# Revit family: BIM_KUBAIR F400 CC INTZ Vertical
name_source: partatom
category: Equipement de génie climatique
revit_build: Autodesk Revit 2016 (Build: 20161004_0715(x64)
units: mm (PartAtom-declared; Revit-internal decimal feet)

## family parameters
Basée sur le plan de construction = Non
Cote de connecteur circulaire = Utiliser le diamètre
Couper avec des vides une fois chargée = Non
Numéro OmniClass = 23.75.00.00
Partagée = Non
Point de calcul de pièce = Oui
Titre OmniClass = Climate Control (HVAC)
Toujours verticalement = Oui
Type d'élément = Normal

## types (75) — shared parameters
Classe_de_protection_electrique = F
Consignes – raccordements aérauliques = Raccorder 1, 2 ou 3 ouies  au refoulement et 1, 2 ou 3 ouies à l’aspiration
Fabricant = VIM
G = 31 mm  [stored 0.101706 ft]
Hauteur_equerre = 200 mm  [stored 0.656168 ft]
IfcExportAs = IfcFan
IfcExportType = IfcFlowMovingDevice
Largeur_equerre = 218 mm  [stored 0.715223 ft]
Lien_page_produit = http://www.vim.fr
Materiau_caisson = Acier, galvanisé
Protection_IP = IP 55
Visibilité_marque = Oui

## per-type parameters (varying)
| type | A | BVC | C | Code_article | Courant_nominal | D | Debit_maxi | Debit_mini | GC | H | L | Modèle | Nombre_de_phases | Poids | Position_A_equerre | Prof_INTZ | Puissance_electrique | Tension_nominale |
| KUBAIR F400 CC 355 6PM INTZ 0,18kW | 627 mm  [stored 2.05709 ft] | 645 mm  [stored 2.11614 ft] | 263 mm  [stored 0.862861 ft] | 644537 | 2 A | 559 mm  [stored 1.83399 ft] | 2140 m³/h | 620 m³/h | 50 mm  [stored 0.164042 ft] | 315 mm  [stored 1.03346 ft] | 321 mm  [stored 1.05315 ft] | KUBAIR F400 CC 355 6PM INTZ 0,18kW Caisson | 1 | 59 Kg | 155 mm  [stored 0.50853 ft] | 100 mm  [stored 0.328084 ft] | 180 W | 230 V |
| KUBAIR F400 CC 355 4PM INTZ 0,25kW | 627 mm  [stored 2.05709 ft] | 645 mm  [stored 2.11614 ft] | 263 mm  [stored 0.862861 ft] | 644533 | 3 A | 559 mm  [stored 1.83399 ft] | 3090 m³/h | 900 m³/h | 50 mm  [stored 0.164042 ft] | 315 mm  [stored 1.03346 ft] | 321 mm  [stored 1.05315 ft] | KUBAIR F400 CC 355 4PM INTZ 0,25kW Caisson | 1 | 59 Kg | 155 mm  [stored 0.50853 ft] | 100 mm  [stored 0.328084 ft] | 250 W | 230 V |
| KUBAIR F400 CC 355 4PT IE1 INTZ 0,25kW | 627 mm  [stored 2.05709 ft] | 645 mm  [stored 2.11614 ft] | 263 mm  [stored 0.862861 ft] | 644541 | 1 A | 559 mm  [stored 1.83399 ft] | 3090 m³/h | 900 m³/h | 50 mm  [stored 0.164042 ft] | 315 mm  [stored 1.03346 ft] | 321 mm  [stored 1.05315 ft] | KUBAIR F400 CC 355 4PT IE1 INTZ 0,25kW Caisson | 3 | 59 Kg | 155 mm  [stored 0.50853 ft] | 100 mm  [stored 0.328084 ft] | 250 W | 400 V |
| KUBAIR F400 CC 355 4PT IE2 INTZ 0,25kW | 627 mm  [stored 2.05709 ft] | 645 mm  [stored 2.11614 ft] | 263 mm  [stored 0.862861 ft] | 644545 | 1 A | 559 mm  [stored 1.83399 ft] | 3090 m³/h | 900 m³/h | 50 mm  [stored 0.164042 ft] | 315 mm  [stored 1.03346 ft] | 321 mm  [stored 1.05315 ft] | KUBAIR F400 CC 355 4PT IE2 INTZ 0,25kW Caisson | 3 | 59 Kg | 155 mm  [stored 0.50853 ft] | 100 mm  [stored 0.328084 ft] | 250 W | 400 V |
| KUBAIR F400 CC 355 4PT IE3 INTZ 0,25kW | 627 mm  [stored 2.05709 ft] | 645 mm  [stored 2.11614 ft] | 263 mm  [stored 0.862861 ft] | 644549 | 1 A | 559 mm  [stored 1.83399 ft] | 3090 m³/h | 900 m³/h | 50 mm  [stored 0.164042 ft] | 315 mm  [stored 1.03346 ft] | 321 mm  [stored 1.05315 ft] | KUBAIR F400 CC 355 4PT IE3 INTZ 0,25kW Caisson | 3 | 59 Kg | 155 mm  [stored 0.50853 ft] | 100 mm  [stored 0.328084 ft] | 250 W | 400 V |
| KUBAIR F400 CC 355 6PT IE1 INTZ 0,18kW | 627 mm  [stored 2.05709 ft] | 645 mm  [stored 2.11614 ft] | 263 mm  [stored 0.862861 ft] | 644553 | 1 A | 559 mm  [stored 1.83399 ft] | 2140 m³/h | 620 m³/h | 50 mm  [stored 0.164042 ft] | 315 mm  [stored 1.03346 ft] | 321 mm  [stored 1.05315 ft] | KUBAIR F400 CC 355 6PT IE1 INTZ 0,18kW Caisson | 3 | 59 Kg | 155 mm  [stored 0.50853 ft] | 100 mm  [stored 0.328084 ft] | 180 W | 400 V |
| KUBAIR F400 CC 355 6PT IE2 INTZ 0,18kW | 627 mm  [stored 2.05709 ft] | 645 mm  [stored 2.11614 ft] | 263 mm  [stored 0.862861 ft] | 644557 | 1 A | 559 mm  [stored 1.83399 ft] | 2140 m³/h | 620 m³/h | 50 mm  [stored 0.164042 ft] | 315 mm  [stored 1.03346 ft] | 321 mm  [stored 1.05315 ft] | KUBAIR F400 CC 355 6PT IE2 INTZ 0,18kW Caisson | 3 | 59 Kg | 155 mm  [stored 0.50853 ft] | 100 mm  [stored 0.328084 ft] | 180 W | 400 V |
| KUBAIR F400 CC 355 6PT IE3 INTZ 0,18kW | 627 mm  [stored 2.05709 ft] | 645 mm  [stored 2.11614 ft] | 263 mm  [stored 0.862861 ft] | 644561 | 1 A | 559 mm  [stored 1.83399 ft] | 2140 m³/h | 620 m³/h | 50 mm  [stored 0.164042 ft] | 315 mm  [stored 1.03346 ft] | 321 mm  [stored 1.05315 ft] | KUBAIR F400 CC 355 6PT IE3 INTZ 0,18kW Caisson | 3 | 59 Kg | 155 mm  [stored 0.50853 ft] | 100 mm  [stored 0.328084 ft] | 180 W | 400 V |
| KUBAIR F400 CC 355 4/6PT INTZ 0,30/0,10kW | 627 mm  [stored 2.05709 ft] | 645 mm  [stored 2.11614 ft] | 263 mm  [stored 0.862861 ft] | 644565 | 1 A | 559 mm  [stored 1.83399 ft] | 3090 m³/h | 900 m³/h | 50 mm  [stored 0.164042 ft] | 315 mm  [stored 1.03346 ft] | 321 mm  [stored 1.05315 ft] | KUBAIR F400 CC 355 4/6PT INTZ 0,30/0,10kW Caisson | 3 | 61 Kg | 155 mm  [stored 0.50853 ft] | 100 mm  [stored 0.328084 ft] | 300 W | 400 V |
| KUBAIR F400 CC 355 4/8PT INTZ 0,60/0,15kW | 627 mm  [stored 2.05709 ft] | 645 mm  [stored 2.11614 ft] | 263 mm  [stored 0.862861 ft] | 644569 | 2 A | 559 mm  [stored 1.83399 ft] | 3090 m³/h | 900 m³/h | 50 mm  [stored 0.164042 ft] | 315 mm  [stored 1.03346 ft] | 321 mm  [stored 1.05315 ft] | KUBAIR F400 CC 355 4/8PT INTZ 0,60/0,15kW Caisson | 3 | 61 Kg | 155 mm  [stored 0.50853 ft] | 100 mm  [stored 0.328084 ft] | 600 W | 400 V |
| KUBAIR F400 CC 400 4PM INTZ 0,55kW | 699 mm  [stored 2.29331 ft] | 678 mm  [stored 2.22441 ft] | 297 mm  [stored 0.974409 ft] | 644573 | 4 A | 631 mm  [stored 2.07021 ft] | 5000 m³/h | 1060 m³/h | 50 mm  [stored 0.164042 ft] | 349 mm  [stored 1.14501 ft] | 321 mm  [stored 1.05315 ft] | KUBAIR F400 CC 400 4PM INTZ 0,55kW Caisson | 1 | 72 Kg | 155 mm  [stored 0.50853 ft] | 120 mm  [stored 0.393701 ft] | 550 W | 230 V |
| KUBAIR F400 CC 400 6PM INTZ 0,25kW | 699 mm  [stored 2.29331 ft] | 678 mm  [stored 2.22441 ft] | 297 mm  [stored 0.974409 ft] | 644577 | 2 A | 631 mm  [stored 2.07021 ft] | 3310 m³/h | 520 m³/h | 50 mm  [stored 0.164042 ft] | 349 mm  [stored 1.14501 ft] | 321 mm  [stored 1.05315 ft] | KUBAIR F400 CC 400 6PM INTZ 0,25kW Caisson | 1 | 72 Kg | 155 mm  [stored 0.50853 ft] | 120 mm  [stored 0.393701 ft] | 250 W | 230 V |
| KUBAIR F400 CC 400 4PT IE1 INTZ 0,55kW | 699 mm  [stored 2.29331 ft] | 678 mm  [stored 2.22441 ft] | 297 mm  [stored 0.974409 ft] | 644581 | 1 A | 631 mm  [stored 2.07021 ft] | 5000 m³/h | 1060 m³/h | 50 mm  [stored 0.164042 ft] | 349 mm  [stored 1.14501 ft] | 321 mm  [stored 1.05315 ft] | KUBAIR F400 CC 400 4PT IE1 INTZ 0,55kW Caisson | 3 | 72 Kg | 155 mm  [stored 0.50853 ft] | 120 mm  [stored 0.393701 ft] | 550 W | 400 V |
| KUBAIR F400 CC 400 4PT IE2 INTZ 0,55kW | 699 mm  [stored 2.29331 ft] | 678 mm  [stored 2.22441 ft] | 297 mm  [stored 0.974409 ft] | 644585 | 1 A | 631 mm  [stored 2.07021 ft] | 5000 m³/h | 1060 m³/h | 50 mm  [stored 0.164042 ft] | 349 mm  [stored 1.14501 ft] | 321 mm  [stored 1.05315 ft] | KUBAIR F400 CC 400 4PT IE2 INTZ 0,55kW Caisson | 3 | 72 Kg | 155 mm  [stored 0.50853 ft] | 120 mm  [stored 0.393701 ft] | 550 W | 400 V |
| KUBAIR F400 CC 400 4PT IE3 INTZ 0,55kW | 699 mm  [stored 2.29331 ft] | 678 mm  [stored 2.22441 ft] | 297 mm  [stored 0.974409 ft] | 644589 | 1 A | 631 mm  [stored 2.07021 ft] | 5000 m³/h | 1060 m³/h | 50 mm  [stored 0.164042 ft] | 349 mm  [stored 1.14501 ft] | 321 mm  [stored 1.05315 ft] | KUBAIR F400 CC 400 4PT IE3 INTZ 0,55kW Caisson | 3 | 72 Kg | 155 mm  [stored 0.50853 ft] | 120 mm  [stored 0.393701 ft] | 550 W | 400 V |
| KUBAIR F400 CC 400 6PT IE1 INTZ 0,37kW | 699 mm  [stored 2.29331 ft] | 678 mm  [stored 2.22441 ft] | 297 mm  [stored 0.974409 ft] | 644593 | 1 A | 631 mm  [stored 2.07021 ft] | 3310 m³/h | 520 m³/h | 50 mm  [stored 0.164042 ft] | 349 mm  [stored 1.14501 ft] | 321 mm  [stored 1.05315 ft] | KUBAIR F400 CC 400 6PT IE1 INTZ 0,37kW Caisson | 3 | 72 Kg | 155 mm  [stored 0.50853 ft] | 120 mm  [stored 0.393701 ft] | 370 W | 400 V |
| KUBAIR F400 CC 400 6PT IE2 INTZ 0,37kW | 699 mm  [stored 2.29331 ft] | 678 mm  [stored 2.22441 ft] | 297 mm  [stored 0.974409 ft] | 644597 | 1 A | 631 mm  [stored 2.07021 ft] | 3310 m³/h | 520 m³/h | 50 mm  [stored 0.164042 ft] | 349 mm  [stored 1.14501 ft] | 321 mm  [stored 1.05315 ft] | KUBAIR F400 CC 400 6PT IE2 INTZ 0,37kW Caisson | 3 | 72 Kg | 155 mm  [stored 0.50853 ft] | 120 mm  [stored 0.393701 ft] | 370 W | 400 V |
| KUBAIR F400 CC 400 6PT IE3 INTZ 0,37kW | 699 mm  [stored 2.29331 ft] | 678 mm  [stored 2.22441 ft] | 297 mm  [stored 0.974409 ft] | 644601 | 1 A | 631 mm  [stored 2.07021 ft] | 3310 m³/h | 520 m³/h | 50 mm  [stored 0.164042 ft] | 349 mm  [stored 1.14501 ft] | 321 mm  [stored 1.05315 ft] | KUBAIR F400 CC 400 6PT IE3 INTZ 0,37kW Caisson | 3 | 72 Kg | 155 mm  [stored 0.50853 ft] | 120 mm  [stored 0.393701 ft] | 370 W | 400 V |
| KUBAIR F400 CC 400 4/6PT INTZ 0,55/0,20kW | 699 mm  [stored 2.29331 ft] | 678 mm  [stored 2.22441 ft] | 297 mm  [stored 0.974409 ft] | 644605 | 2 A | 631 mm  [stored 2.07021 ft] | 5000 m³/h | 1060 m³/h | 50 mm  [stored 0.164042 ft] | 349 mm  [stored 1.14501 ft] | 321 mm  [stored 1.05315 ft] | KUBAIR F400 CC 400 4/6PT INTZ 0,55/0,20kW Caisson | 3 | 74 Kg | 155 mm  [stored 0.50853 ft] | 120 mm  [stored 0.393701 ft] | 550 W | 400 V |
| KUBAIR F400 CC 400 4/8PT INTZ 0,60/0,15kW | 699 mm  [stored 2.29331 ft] | 678 mm  [stored 2.22441 ft] | 297 mm  [stored 0.974409 ft] | 644609 | 2 A | 631 mm  [stored 2.07021 ft] | 5000 m³/h | 1060 m³/h | 50 mm  [stored 0.164042 ft] | 349 mm  [stored 1.14501 ft] | 321 mm  [stored 1.05315 ft] | KUBAIR F400 CC 400 4/8PT INTZ 0,60/0,15kW Caisson | 3 | 74 Kg | 155 mm  [stored 0.50853 ft] | 120 mm  [stored 0.393701 ft] | 600 W | 400 V |
| KUBAIR F400 CC 450 6PM INTZ 0,25kW | 779 mm  [stored 2.55577 ft] | 738 mm  [stored 2.42126 ft] | 326 mm  [stored 1.06955 ft] | 644613 | 2 A | 711 mm  [stored 2.33268 ft] | 4750 m³/h | 820 m³/h | 50 mm  [stored 0.164042 ft] | 378 mm | 321 mm  [stored 1.05315 ft] | KUBAIR F400 CC 450 6PM INTZ 0,25kW Caisson | 1 | 92 Kg | 175 mm | 120 mm  [stored 0.393701 ft] | 250 W | 230 V |
| KUBAIR F400 CC 450 4PT IE2 INTZ 1,1kW | 779 mm  [stored 2.55577 ft] | 738 mm  [stored 2.42126 ft] | 326 mm  [stored 1.06955 ft] | 644617 | 2 A | 711 mm  [stored 2.33268 ft] | 7080 m³/h | 1230 m³/h | 50 mm  [stored 0.164042 ft] | 378 mm | 321 mm  [stored 1.05315 ft] | KUBAIR F400 CC 450 4PT IE2 INTZ 1,1kW Caisson | 3 | 92 Kg | 175 mm | 120 mm  [stored 0.393701 ft] | 1100 W | 400 V |
| KUBAIR F400 CC 450 4PT IE3 INTZ 1,1kW | 779 mm  [stored 2.55577 ft] | 738 mm  [stored 2.42126 ft] | 326 mm  [stored 1.06955 ft] | 644621 | 2 A | 711 mm  [stored 2.33268 ft] | 7080 m³/h | 1230 m³/h | 50 mm  [stored 0.164042 ft] | 378 mm | 321 mm  [stored 1.05315 ft] | KUBAIR F400 CC 450 4PT IE3 INTZ 1,1kW Caisson | 3 | 92 Kg | 175 mm | 120 mm  [stored 0.393701 ft] | 1100 W | 400 V |
| KUBAIR F400 CC 450 6PT IE1 INTZ 0,37kW | 779 mm  [stored 2.55577 ft] | 738 mm  [stored 2.42126 ft] | 326 mm  [stored 1.06955 ft] | 644625 | 1 A | 711 mm  [stored 2.33268 ft] | 4750 m³/h | 820 m³/h | 50 mm  [stored 0.164042 ft] | 378 mm | 321 mm  [stored 1.05315 ft] | KUBAIR F400 CC 450 6PT IE1 INTZ 0,37kW Caisson | 3 | 92 Kg | 175 mm | 120 mm  [stored 0.393701 ft] | 370 W | 400 V |
| KUBAIR F400 CC 450 6PT IE2 INTZ 0,37kW | 779 mm  [stored 2.55577 ft] | 738 mm  [stored 2.42126 ft] | 326 mm  [stored 1.06955 ft] | 644629 | 1 A | 711 mm  [stored 2.33268 ft] | 4750 m³/h | 820 m³/h | 50 mm  [stored 0.164042 ft] | 378 mm | 321 mm  [stored 1.05315 ft] | KUBAIR F400 CC 450 6PT IE2 INTZ 0,37kW Caisson | 3 | 92 Kg | 175 mm | 120 mm  [stored 0.393701 ft] | 370 W | 400 V |
| KUBAIR F400 CC 450 6PT IE3 INTZ 0,37kW | 779 mm  [stored 2.55577 ft] | 738 mm  [stored 2.42126 ft] | 326 mm  [stored 1.06955 ft] | 644633 | 1 A | 711 mm  [stored 2.33268 ft] | 4750 m³/h | 820 m³/h | 50 mm  [stored 0.164042 ft] | 378 mm | 321 mm  [stored 1.05315 ft] | KUBAIR F400 CC 450 6PT IE3 INTZ 0,37kW Caisson | 3 | 92 Kg | 175 mm | 120 mm  [stored 0.393701 ft] | 370 W | 400 V |
| KUBAIR F400 CC 450 8PT IE1 INTZ 0,18kW | 779 mm  [stored 2.55577 ft] | 738 mm  [stored 2.42126 ft] | 326 mm  [stored 1.06955 ft] | 644637 | 1 A | 711 mm  [stored 2.33268 ft] | 3420 m³/h | 590 m³/h | 50 mm  [stored 0.164042 ft] | 378 mm | 321 mm  [stored 1.05315 ft] | KUBAIR F400 CC 450 8PT IE1 INTZ 0,18kW Caisson | 3 | 92 Kg | 175 mm | 120 mm  [stored 0.393701 ft] | 180 W | 400 V |
| KUBAIR F400 CC 450 8PT IE2 INTZ 0,18kW | 779 mm  [stored 2.55577 ft] | 738 mm  [stored 2.42126 ft] | 326 mm  [stored 1.06955 ft] | 644641 | 1 A | 711 mm  [stored 2.33268 ft] | 3420 m³/h | 590 m³/h | 50 mm  [stored 0.164042 ft] | 378 mm | 321 mm  [stored 1.05315 ft] | KUBAIR F400 CC 450 8PT IE2 INTZ 0,18kW Caisson | 3 | 92 Kg | 175 mm | 120 mm  [stored 0.393701 ft] | 180 W | 400 V |
| KUBAIR F400 CC 450 8PT IE3 INTZ 0,18kW | 779 mm  [stored 2.55577 ft] | 738 mm  [stored 2.42126 ft] | 326 mm  [stored 1.06955 ft] | 644645 | 1 A | 711 mm  [stored 2.33268 ft] | 3420 m³/h | 590 m³/h | 50 mm  [stored 0.164042 ft] | 378 mm | 321 mm  [stored 1.05315 ft] | KUBAIR F400 CC 450 8PT IE3 INTZ 0,18kW Caisson | 3 | 92 Kg | 175 mm | 120 mm  [stored 0.393701 ft] | 180 W | 400 V |
| KUBAIR F400 CC 450 4/6PT INTZ 1,10/0,30kW | 779 mm  [stored 2.55577 ft] | 738 mm  [stored 2.42126 ft] | 326 mm  [stored 1.06955 ft] | 644649 | 3 A | 711 mm  [stored 2.33268 ft] | 7080 m³/h | 1230 m³/h | 50 mm  [stored 0.164042 ft] | 378 mm | 321 mm  [stored 1.05315 ft] | KUBAIR F400 CC 450 4/6PT INTZ 1,10/0,30kW Caisson | 3 | 94 Kg | 175 mm | 120 mm  [stored 0.393701 ft] | 1100 W | 400 V |
| KUBAIR F400 CC 450 4/8PT INTZ 1,20/0,30kW | 779 mm  [stored 2.55577 ft] | 738 mm  [stored 2.42126 ft] | 326 mm  [stored 1.06955 ft] | 644653 | 3 A | 711 mm  [stored 2.33268 ft] | 7080 m³/h | 1230 m³/h | 50 mm  [stored 0.164042 ft] | 378 mm | 321 mm  [stored 1.05315 ft] | KUBAIR F400 CC 450 4/8PT INTZ 1,20/0,30kW Caisson | 3 | 94 Kg | 175 mm | 120 mm  [stored 0.393701 ft] | 1200 W | 400 V |
| KUBAIR F400 CC 450 6/8PT INTZ 0,37/0,20kW | 779 mm  [stored 2.55577 ft] | 738 mm  [stored 2.42126 ft] | 326 mm  [stored 1.06955 ft] | 644657 | 1 A | 711 mm  [stored 2.33268 ft] | 4750 m³/h | 820 m³/h | 50 mm  [stored 0.164042 ft] | 378 mm | 321 mm  [stored 1.05315 ft] | KUBAIR F400 CC 450 6/8PT INTZ 0,37/0,20kW Caisson | 3 | 94 Kg | 175 mm | 120 mm  [stored 0.393701 ft] | 370 W | 400 V |
| KUBAIR F400 CC 500 6PM INTZ 0,37kW | 858 mm | 784 mm | 338 mm  [stored 1.10892 ft] | 644661 | 3 A | 768 mm  [stored 2.51969 ft] | 5960 m³/h | 920 m³/h | 62 mm  [stored 0.203412 ft] | 402 mm  [stored 1.3189 ft] | 351 mm | KUBAIR F400 CC 500 6PM INTZ 0,37kW Caisson | 1 | 114 Kg | 175 mm | 120 mm  [stored 0.393701 ft] | 370 W | 230 V |
| KUBAIR F400 CC 500 4PT IE2 INTZ 1,5kW | 858 mm | 784 mm | 338 mm  [stored 1.10892 ft] | 644665 | 3 A | 768 mm  [stored 2.51969 ft] | 8850 m³/h | 1370 m³/h | 62 mm  [stored 0.203412 ft] | 402 mm  [stored 1.3189 ft] | 351 mm | KUBAIR F400 CC 500 4PT IE2 INTZ 1,5kW Caisson | 3 | 114 Kg | 175 mm | 120 mm  [stored 0.393701 ft] | 1500 W | 400 V |
| KUBAIR F400 CC 500 4PT IE3 INTZ 1,5kW | 858 mm | 784 mm | 338 mm  [stored 1.10892 ft] | 644669 | 3 A | 768 mm  [stored 2.51969 ft] | 8850 m³/h | 1370 m³/h | 62 mm  [stored 0.203412 ft] | 402 mm  [stored 1.3189 ft] | 351 mm | KUBAIR F400 CC 500 4PT IE3 INTZ 1,5kW Caisson | 3 | 114 Kg | 175 mm | 120 mm  [stored 0.393701 ft] | 1500 W | 400 V |
| KUBAIR F400 CC 500 6PT IE1 INTZ 0,55kW | 858 mm | 784 mm | 338 mm  [stored 1.10892 ft] | 644673 | 2 A | 768 mm  [stored 2.51969 ft] | 5960 m³/h | 920 m³/h | 62 mm  [stored 0.203412 ft] | 402 mm  [stored 1.3189 ft] | 351 mm | KUBAIR F400 CC 500 6PT IE1 INTZ 0,55kW Caisson | 3 | 114 Kg | 175 mm | 120 mm  [stored 0.393701 ft] | 550 W | 400 V |
| KUBAIR F400 CC 500 6PT IE2 INTZ 0,55kW | 858 mm | 784 mm | 338 mm  [stored 1.10892 ft] | 644677 | 1 A | 768 mm  [stored 2.51969 ft] | 5960 m³/h | 920 m³/h | 62 mm  [stored 0.203412 ft] | 402 mm  [stored 1.3189 ft] | 351 mm | KUBAIR F400 CC 500 6PT IE2 INTZ 0,55kW Caisson | 3 | 114 Kg | 175 mm | 120 mm  [stored 0.393701 ft] | 550 W | 400 V |
| KUBAIR F400 CC 500 6PT IE3 INTZ 0,55kW | 858 mm | 784 mm | 338 mm  [stored 1.10892 ft] | 644681 | 1 A | 768 mm  [stored 2.51969 ft] | 5960 m³/h | 920 m³/h | 62 mm  [stored 0.203412 ft] | 402 mm  [stored 1.3189 ft] | 351 mm | KUBAIR F400 CC 500 6PT IE3 INTZ 0,55kW Caisson | 3 | 114 Kg | 175 mm | 120 mm  [stored 0.393701 ft] | 550 W | 400 V |
| KUBAIR F400 CC 500 8PT IE1 INTZ 0,18kW | 858 mm | 784 mm | 338 mm  [stored 1.10892 ft] | 644685 | 1 A | 768 mm  [stored 2.51969 ft] | 4280 m³/h | 660 m³/h | 62 mm  [stored 0.203412 ft] | 402 mm  [stored 1.3189 ft] | 351 mm | KUBAIR F400 CC 500 8PT IE1 INTZ 0,18kW Caisson | 3 | 114 Kg | 175 mm | 120 mm  [stored 0.393701 ft] | 180 W | 400 V |
| KUBAIR F400 CC 500 8PT IE2 INTZ 0,18kW | 858 mm | 784 mm | 338 mm  [stored 1.10892 ft] | 644689 | 1 A | 768 mm  [stored 2.51969 ft] | 4280 m³/h | 660 m³/h | 62 mm  [stored 0.203412 ft] | 402 mm  [stored 1.3189 ft] | 351 mm | KUBAIR F400 CC 500 8PT IE2 INTZ 0,18kW Caisson | 3 | 114 Kg | 175 mm | 120 mm  [stored 0.393701 ft] | 180 W | 400 V |
| KUBAIR F400 CC 500 8PT IE3 INTZ 0,18kW | 858 mm | 784 mm | 338 mm  [stored 1.10892 ft] | 644693 | 1 A | 768 mm  [stored 2.51969 ft] | 4280 m³/h | 660 m³/h | 62 mm  [stored 0.203412 ft] | 402 mm  [stored 1.3189 ft] | 351 mm | KUBAIR F400 CC 500 8PT IE3 INTZ 0,18kW Caisson | 3 | 114 Kg | 175 mm | 120 mm  [stored 0.393701 ft] | 180 W | 400 V |
| KUBAIR F400 CC 500 4/6PT INTZ 1,50/0,37kW | 858 mm | 784 mm | 338 mm  [stored 1.10892 ft] | 644697 | 4 A | 768 mm  [stored 2.51969 ft] | 8850 m³/h | 1370 m³/h | 62 mm  [stored 0.203412 ft] | 402 mm  [stored 1.3189 ft] | 351 mm | KUBAIR F400 CC 500 4/6PT INTZ 1,50/0,37kW Caisson | 3 | 116 Kg | 175 mm | 120 mm  [stored 0.393701 ft] | 1500 W | 400 V |
| KUBAIR F400 CC 500 4/8PT INTZ 1,60/0,40kW | 858 mm | 784 mm | 338 mm  [stored 1.10892 ft] | 644701 | 4 A | 768 mm  [stored 2.51969 ft] | 8850 m³/h | 1370 m³/h | 62 mm  [stored 0.203412 ft] | 402 mm  [stored 1.3189 ft] | 351 mm | KUBAIR F400 CC 500 4/8PT INTZ 1,60/0,40kW Caisson | 3 | 116 Kg | 175 mm | 120 mm  [stored 0.393701 ft] | 1600 W | 400 V |
| KUBAIR F400 CC 500 6/8PT INTZ 0,55/0,37kW | 858 mm | 784 mm | 338 mm  [stored 1.10892 ft] | 644705 | 2 A | 768 mm  [stored 2.51969 ft] | 5960 m³/h | 920 m³/h | 62 mm  [stored 0.203412 ft] | 402 mm  [stored 1.3189 ft] | 351 mm | KUBAIR F400 CC 500 6/8PT INTZ 0,55/0,37kW Caisson | 3 | 116 Kg | 175 mm | 120 mm  [stored 0.393701 ft] | 550 W | 400 V |
| KUBAIR F400 CC 560 4PT IE2 INTZ 2,2kW | 954 mm | 817 mm | 354 mm | 644709 | 5 A | 864 mm | 11330 m³/h | 1520 m³/h | 62 mm  [stored 0.203412 ft] | 419 mm  [stored 1.37467 ft] | 351 mm | KUBAIR F400 CC 560 4PT IE2 INTZ 2,2kW Caisson | 3 | 159 Kg | 213 mm | 120 mm  [stored 0.393701 ft] | 2200 W | 400 V |
| KUBAIR F400 CC 560 4PT IE3 INTZ 2,2kW | 954 mm | 817 mm | 354 mm | 644713 | 5 A | 864 mm | 11330 m³/h | 1520 m³/h | 62 mm  [stored 0.203412 ft] | 419 mm  [stored 1.37467 ft] | 351 mm | KUBAIR F400 CC 560 4PT IE3 INTZ 2,2kW Caisson | 3 | 159 Kg | 213 mm | 120 mm  [stored 0.393701 ft] | 2200 W | 400 V |
| KUBAIR F400 CC 560 6PT IE2 INTZ 0,75kW | 954 mm | 817 mm | 354 mm | 644717 | 2 A | 864 mm | 7630 m³/h | 1020 m³/h | 62 mm  [stored 0.203412 ft] | 419 mm  [stored 1.37467 ft] | 351 mm | KUBAIR F400 CC 560 6PT IE2 INTZ 0,75kW Caisson | 3 | 159 Kg | 213 mm | 120 mm  [stored 0.393701 ft] | 750 W | 400 V |
| KUBAIR F400 CC 560 6PT IE3 INTZ 0,75kW | 954 mm | 817 mm | 354 mm | 644721 | 2 A | 864 mm | 7630 m³/h | 1020 m³/h | 62 mm  [stored 0.203412 ft] | 419 mm  [stored 1.37467 ft] | 351 mm | KUBAIR F400 CC 560 6PT IE3 INTZ 0,75kW Caisson | 3 | 159 Kg | 213 mm | 120 mm  [stored 0.393701 ft] | 750 W | 400 V |
| KUBAIR F400 CC 560 8PT IE1 INTZ 0,37kW | 954 mm | 817 mm | 354 mm | 644725 | 1 A | 864 mm | 5490 m³/h | 740 m³/h | 62 mm  [stored 0.203412 ft] | 419 mm  [stored 1.37467 ft] | 351 mm | KUBAIR F400 CC 560 8PT IE1 INTZ 0,37kW Caisson | 3 | 159 Kg | 213 mm | 120 mm  [stored 0.393701 ft] | 370 W | 400 V |
| KUBAIR F400 CC 560 8PT IE2 INTZ 0,37kW | 954 mm | 817 mm | 354 mm | 644729 | 1 A | 864 mm | 5490 m³/h | 740 m³/h | 62 mm  [stored 0.203412 ft] | 419 mm  [stored 1.37467 ft] | 351 mm | KUBAIR F400 CC 560 8PT IE2 INTZ 0,37kW Caisson | 3 | 159 Kg | 213 mm | 120 mm  [stored 0.393701 ft] | 370 W | 400 V |
| KUBAIR F400 CC 560 8PT IE3 INTZ 0,37kW | 954 mm | 817 mm | 354 mm | 644733 | 1 A | 864 mm | 5490 m³/h | 740 m³/h | 62 mm  [stored 0.203412 ft] | 419 mm  [stored 1.37467 ft] | 351 mm | KUBAIR F400 CC 560 8PT IE3 INTZ 0,37kW Caisson | 3 | 159 Kg | 213 mm | 120 mm  [stored 0.393701 ft] | 370 W | 400 V |
| KUBAIR F400 CC 560 4/6PT INTZ 2,20/0,70kW | 954 mm | 817 mm | 354 mm | 644737 | 5 A | 864 mm | 11330 m³/h | 1520 m³/h | 62 mm  [stored 0.203412 ft] | 419 mm  [stored 1.37467 ft] | 351 mm | KUBAIR F400 CC 560 4/6PT INTZ 2,20/0,70kW Caisson | 3 | 161 Kg | 213 mm | 120 mm  [stored 0.393701 ft] | 2200 W | 400 V |
| KUBAIR F400 CC 560 4/8PT INTZ 2,20/0,55kW | 954 mm | 817 mm | 354 mm | 644741 | 5 A | 864 mm | 11330 m³/h | 1520 m³/h | 62 mm  [stored 0.203412 ft] | 419 mm  [stored 1.37467 ft] | 351 mm | KUBAIR F400 CC 560 4/8PT INTZ 2,20/0,55kW Caisson | 3 | 161 Kg | 213 mm | 120 mm  [stored 0.393701 ft] | 2200 W | 400 V |
| KUBAIR F400 CC 560 6/8PT INTZ 0,75/0,37kW | 954 mm | 817 mm | 354 mm | 644745 | 2 A | 864 mm | 7630 m³/h | 1020 m³/h | 62 mm  [stored 0.203412 ft] | 419 mm  [stored 1.37467 ft] | 351 mm | KUBAIR F400 CC 560 6/8PT INTZ 0,75/0,37kW Caisson | 3 | 161 Kg | 213 mm | 120 mm  [stored 0.393701 ft] | 750 W | 400 V |
| KUBAIR F400 CC 630 6PT IE2 INTZ 1,1kW | 1066 mm | 912 mm | 403 mm  [stored 1.32218 ft] | 644749 | 3 A | 977 mm | 10000 m³/h | 1150 m³/h | 62 mm  [stored 0.203412 ft] | 466 mm  [stored 1.52887 ft] | 351 mm | KUBAIR F400 CC 630 6PT IE2 INTZ 1,1kW Caisson | 3 | 162 Kg | 213 mm | 120 mm  [stored 0.393701 ft] | 1100 W | 400 V |
| KUBAIR F400 CC 630 6PT IE3 INTZ 1,1kW | 1066 mm | 912 mm | 403 mm  [stored 1.32218 ft] | 644753 | 3 A | 977 mm | 10000 m³/h | 1150 m³/h | 62 mm  [stored 0.203412 ft] | 466 mm  [stored 1.52887 ft] | 351 mm | KUBAIR F400 CC 630 6PT IE3 INTZ 1,1kW Caisson | 3 | 162 Kg | 213 mm | 120 mm  [stored 0.393701 ft] | 1100 W | 400 V |
| KUBAIR F400 CC 630 8PT IE1 INTZ 0,55kW | 1066 mm | 912 mm | 403 mm  [stored 1.32218 ft] | 644757 | 2 A | 977 mm | 7270 m³/h | 860 m³/h | 62 mm  [stored 0.203412 ft] | 466 mm  [stored 1.52887 ft] | 351 mm | KUBAIR F400 CC 630 8PT IE1 INTZ 0,55kW Caisson | 3 | 163 Kg | 213 mm | 120 mm  [stored 0.393701 ft] | 550 W | 400 V |
| KUBAIR F400 CC 630 8PT IE2 INTZ 0,55kW | 1066 mm | 912 mm | 403 mm  [stored 1.32218 ft] | 644761 | 2 A | 977 mm | 7270 m³/h | 860 m³/h | 62 mm  [stored 0.203412 ft] | 466 mm  [stored 1.52887 ft] | 351 mm | KUBAIR F400 CC 630 8PT IE2 INTZ 0,55kW Caisson | 3 | 163 Kg | 213 mm | 120 mm  [stored 0.393701 ft] | 550 W | 400 V |
| KUBAIR F400 CC 630 8PT IE3 INTZ 0,55kW | 1066 mm | 912 mm | 403 mm  [stored 1.32218 ft] | 644765 | 2 A | 977 mm | 7270 m³/h | 860 m³/h | 62 mm  [stored 0.203412 ft] | 466 mm  [stored 1.52887 ft] | 351 mm | KUBAIR F400 CC 630 8PT IE3 INTZ 0,55kW Caisson | 3 | 163 Kg | 213 mm | 120 mm  [stored 0.393701 ft] | 550 W | 400 V |
| KUBAIR F400 CC 630 6/8PT INTZ 1,10/0,55kW | 1066 mm | 912 mm | 403 mm  [stored 1.32218 ft] | 644769 | 4 A | 977 mm | 10000 m³/h | 1150 m³/h | 62 mm  [stored 0.203412 ft] | 466 mm  [stored 1.52887 ft] | 351 mm | KUBAIR F400 CC 630 6/8PT INTZ 1,10/0,55kW Caisson | 3 | 164 Kg | 213 mm | 120 mm  [stored 0.393701 ft] | 1100 W | 400 V |
| KUBAIR F400 CC 630 6/12PT INTZ 1,10/0,22kW | 1066 mm | 912 mm | 403 mm  [stored 1.32218 ft] | 644773 | 4 A | 977 mm | 10000 m³/h | 1150 m³/h | 62 mm  [stored 0.203412 ft] | 466 mm  [stored 1.52887 ft] | 351 mm | KUBAIR F400 CC 630 6/12PT INTZ 1,10/0,22kW Caisson | 3 | 164 Kg | 213 mm | 120 mm  [stored 0.393701 ft] | 1100 W | 400 V |
| KUBAIR F400 CC 710 6PT IE2 INTZ 3,0kW | 1194 mm | 1032 mm | 462 mm  [stored 1.51575 ft] | 644777 | 7 A | 1104 mm | 18900 m³/h | 420 m³/h | 62 mm  [stored 0.203412 ft] | 526 mm  [stored 1.72572 ft] | 446 mm  [stored 1.46325 ft] | KUBAIR F400 CC 710 6PT IE2 INTZ 3,0kW Caisson | 3 | 264 Kg | 234 mm  [stored 0.767717 ft] | 120 mm  [stored 0.393701 ft] | 3000 W | 400 V |
| KUBAIR F400 CC 710 6PT IE3 INTZ 3,0kW | 1194 mm | 1032 mm | 462 mm  [stored 1.51575 ft] | 644781 | 7 A | 1104 mm | 18900 m³/h | 420 m³/h | 62 mm  [stored 0.203412 ft] | 526 mm  [stored 1.72572 ft] | 446 mm  [stored 1.46325 ft] | KUBAIR F400 CC 710 6PT IE3 INTZ 3,0kW Caisson | 3 | 264 Kg | 234 mm  [stored 0.767717 ft] | 120 mm  [stored 0.393701 ft] | 3000 W | 400 V |
| KUBAIR F400 CC 710 8PT IE1 INTZ 2,2kW | 1194 mm | 1032 mm | 462 mm  [stored 1.51575 ft] | 644785 | 5 A | 1104 mm | 13600 m³/h | 300 m³/h | 62 mm  [stored 0.203412 ft] | 526 mm  [stored 1.72572 ft] | 446 mm  [stored 1.46325 ft] | KUBAIR F400 CC 710 8PT IE1 INTZ 2,2kW Caisson | 3 | 265 Kg | 234 mm  [stored 0.767717 ft] | 120 mm  [stored 0.393701 ft] | 2200 W | 400 V |
| KUBAIR F400 CC 710 8PT IE2 INTZ 2,2kW | 1194 mm | 1032 mm | 462 mm  [stored 1.51575 ft] | 644789 | 5 A | 1104 mm | 13600 m³/h | 300 m³/h | 62 mm  [stored 0.203412 ft] | 526 mm  [stored 1.72572 ft] | 446 mm  [stored 1.46325 ft] | KUBAIR F400 CC 710 8PT IE2 INTZ 2,2kW Caisson | 3 | 265 Kg | 234 mm  [stored 0.767717 ft] | 120 mm  [stored 0.393701 ft] | 2200 W | 400 V |
| KUBAIR F400 CC 710 8PT IE3 INTZ 2,2kW | 1194 mm | 1032 mm | 462 mm  [stored 1.51575 ft] | 644793 | 5 A | 1104 mm | 13600 m³/h | 300 m³/h | 62 mm  [stored 0.203412 ft] | 526 mm  [stored 1.72572 ft] | 446 mm  [stored 1.46325 ft] | KUBAIR F400 CC 710 8PT IE3 INTZ 2,2kW Caisson | 3 | 265 Kg | 234 mm  [stored 0.767717 ft] | 120 mm  [stored 0.393701 ft] | 2200 W | 400 V |
| KUBAIR F400 CC 710 6/8PT INTZ 3,00/0,75kW | 1194 mm | 1032 mm | 462 mm  [stored 1.51575 ft] | 644797 | 8 A | 1104 mm | 18900 m³/h | 420 m³/h | 62 mm  [stored 0.203412 ft] | 526 mm  [stored 1.72572 ft] | 446 mm  [stored 1.46325 ft] | KUBAIR F400 CC 710 6/8PT INTZ 3,00/0,75kW Caisson | 3 | 266 Kg | 234 mm  [stored 0.767717 ft] | 120 mm  [stored 0.393701 ft] | 3000 W | 400 V |
| KUBAIR F400 CC 710 6/12PT INTZ 4,0/1,0kW | 1194 mm | 1032 mm | 462 mm  [stored 1.51575 ft] | 644801 | 13 A | 1104 mm | 18900 m³/h | 420 m³/h | 62 mm  [stored 0.203412 ft] | 526 mm  [stored 1.72572 ft] | 446 mm  [stored 1.46325 ft] | KUBAIR F400 CC 710 6/12PT INTZ 4,0/1,0kW Caisson | 3 | 266 Kg | 234 mm  [stored 0.767717 ft] | 120 mm  [stored 0.393701 ft] | 4000 W | 400 V |
| KUBAIR F400 CC 800 6PT IE2 INTZ 4,0kW | 1338 mm | 1084 mm | 488 mm  [stored 1.60105 ft] | 644805 | 9 A | 1248 mm | 23390 m³/h | 660 m³/h | 62 mm  [stored 0.203412 ft] | 552 mm  [stored 1.81102 ft] | 446 mm  [stored 1.46325 ft] | KUBAIR F400 CC 800 6PT IE2 INTZ 4,0kW Caisson | 3 | 307 Kg | 234 mm  [stored 0.767717 ft] | 120 mm  [stored 0.393701 ft] | 4000 W | 400 V |
| KUBAIR F400 CC 800 6PT IE3 INTZ 4,0kW | 1338 mm | 1084 mm | 488 mm  [stored 1.60105 ft] | 644809 | 9 A | 1248 mm | 23390 m³/h | 660 m³/h | 62 mm  [stored 0.203412 ft] | 552 mm  [stored 1.81102 ft] | 446 mm  [stored 1.46325 ft] | KUBAIR F400 CC 800 6PT IE3 INTZ 4,0kW Caisson | 3 | 307 Kg | 234 mm  [stored 0.767717 ft] | 120 mm  [stored 0.393701 ft] | 4000 W | 400 V |
| KUBAIR F400 CC 800 8PT IE1 INTZ 2,2kW | 1338 mm | 1084 mm | 488 mm  [stored 1.60105 ft] | 644813 | 5 A | 1248 mm | 16910 m³/h | 480 m³/h | 62 mm  [stored 0.203412 ft] | 552 mm  [stored 1.81102 ft] | 446 mm  [stored 1.46325 ft] | KUBAIR F400 CC 800 8PT IE1 INTZ 2,2kW Caisson | 3 | 308 Kg | 234 mm  [stored 0.767717 ft] | 120 mm  [stored 0.393701 ft] | 2200 W | 400 V |
| KUBAIR F400 CC 800 8PT IE2 INTZ 2,2kW | 1338 mm | 1084 mm | 488 mm  [stored 1.60105 ft] | 644817 | 5 A | 1248 mm | 16910 m³/h | 480 m³/h | 62 mm  [stored 0.203412 ft] | 552 mm  [stored 1.81102 ft] | 446 mm  [stored 1.46325 ft] | KUBAIR F400 CC 800 8PT IE2 INTZ 2,2kW Caisson | 3 | 308 Kg | 234 mm  [stored 0.767717 ft] | 120 mm  [stored 0.393701 ft] | 2200 W | 400 V |
| KUBAIR F400 CC 800 8PT IE3 INTZ 2,2kW | 1338 mm | 1084 mm | 488 mm  [stored 1.60105 ft] | 644821 | 5 A | 1248 mm | 16910 m³/h | 480 m³/h | 62 mm  [stored 0.203412 ft] | 552 mm  [stored 1.81102 ft] | 446 mm  [stored 1.46325 ft] | KUBAIR F400 CC 800 8PT IE3 INTZ 2,2kW Caisson | 3 | 308 Kg | 234 mm  [stored 0.767717 ft] | 120 mm  [stored 0.393701 ft] | 2200 W | 400 V |
| KUBAIR F400 CC 800 6/8PT INTZ 4,0/1,1kW | 1338 mm | 1084 mm | 488 mm  [stored 1.60105 ft] | 644825 | 16 A | 1248 mm | 23390 m³/h | 660 m³/h | 62 mm  [stored 0.203412 ft] | 552 mm  [stored 1.81102 ft] | 446 mm  [stored 1.46325 ft] | KUBAIR F400 CC 800 6/8PT INTZ 4,0/1,1kW Caisson | 3 | 309 Kg | 234 mm  [stored 0.767717 ft] | 120 mm  [stored 0.393701 ft] | 4000 W | 400 V |
| KUBAIR F400 CC 800 6/12PT INTZ 4,0/1,0kW | 1338 mm | 1084 mm | 488 mm  [stored 1.60105 ft] | 644829 | 13 A | 1248 mm | 23390 m³/h | 660 m³/h | 62 mm  [stored 0.203412 ft] | 552 mm  [stored 1.81102 ft] | 446 mm  [stored 1.46325 ft] | KUBAIR F400 CC 800 6/12PT INTZ 4,0/1,0kW Caisson | 3 | 309 Kg | 234 mm  [stored 0.767717 ft] | 120 mm  [stored 0.393701 ft] | 4000 W | 400 V |

note: [stored X ft] marks values corroborated as IEEE doubles in the binary element streams (Revit-internal decimal feet)

## geometry (parser evidence)
native form markers: Blend x12
no freeform markers — native parametric forms only
